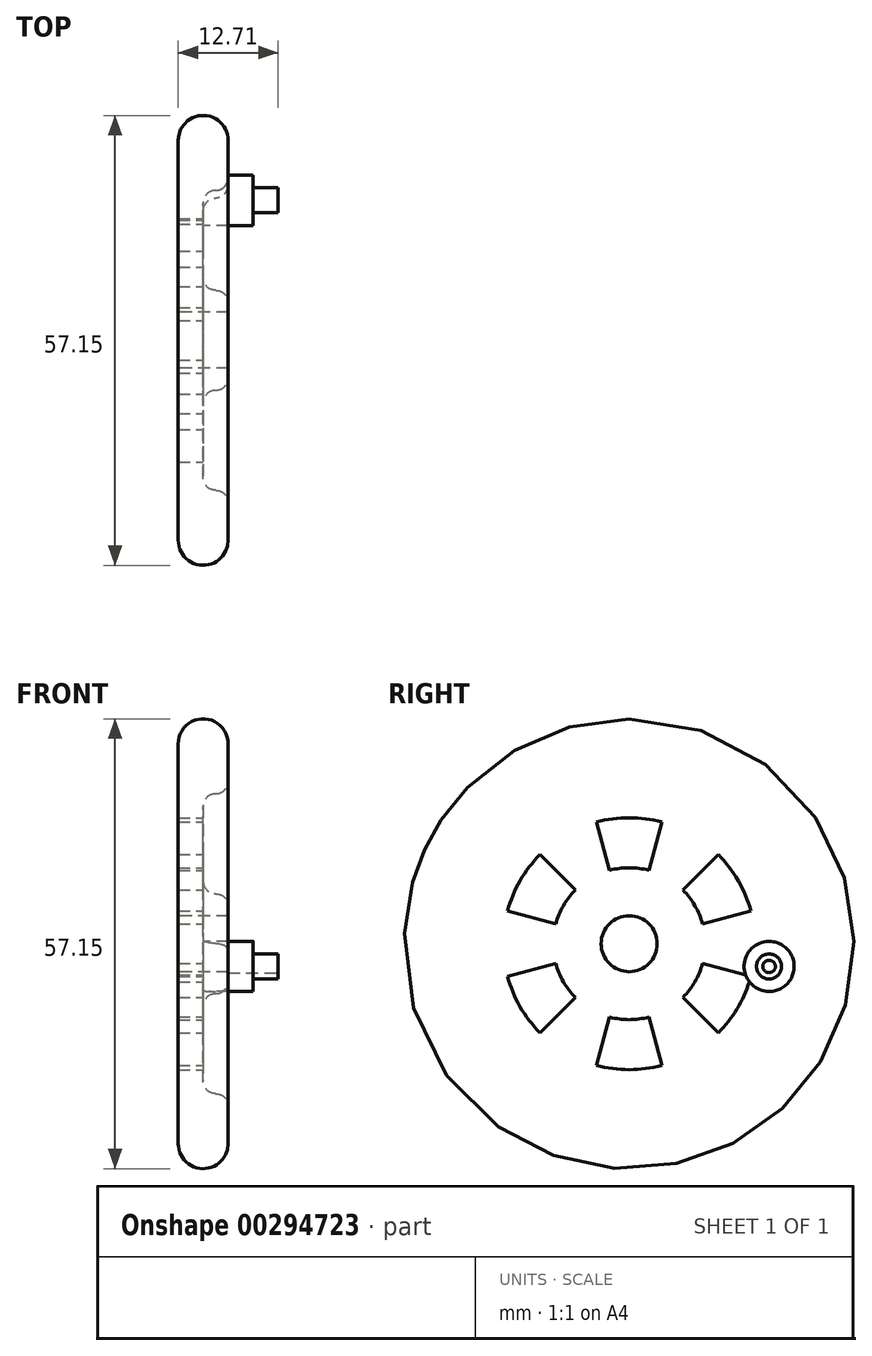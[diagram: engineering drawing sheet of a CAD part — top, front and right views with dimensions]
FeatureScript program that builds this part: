
annotation { "Feature Type Name" : "Feature", "Feature Type Description" : "" }
export const myFeature = defineFeature(function(context is Context, id is Id, definition is map)
    precondition{}
    {
        {
            var Q0;
            Q0=qCreatedBy(makeId("Top.planeOp"),FACE);
            var sketch = newSketch(context, id + "F0", { "sketchPlane" : qUnion([Q0])});
            skArc(sketch, "E0", {"start": v(-3.18, -11.95) * mm, "mid": v(0, -15.13) * mm, "end": v(3.18, -11.95) * mm});
            skLineSegment(sketch, "E1", {"start": v(0, 5.5) * mm, "end": v(0, -4) * mm});
            skLineSegment(sketch, "E2", {"start": v(1.6, -5.6) * mm, "end": v(3.18, -5.6) * mm});
            skLineSegment(sketch, "E3", {"start": v(3.18, -5.6) * mm, "end": v(3.18, -11.95) * mm});
            skLineSegment(sketch, "E4", {"start": v(-3.18, 9.9) * mm, "end": v(-3.18, 11.85) * mm, "construction": true});
            skLineSegment(sketch, "E5", {"start": v(-1.57, 13.45) * mm, "end": v(3.18, 13.45) * mm, "construction": true});
            skLineSegment(sketch, "E6", {"start": v(3.17, 13.45) * mm, "end": v(3.17, 9.9) * mm, "construction": true});
            skPoint(sketch, "E7.visualSharp", {"position": v(-3.18, 9.9) * mm});
            skPoint(sketch, "E8.visualSharp", {"position": v(0, -5.6) * mm});
            skArc(sketch, "E8.filletArc", {"start": v(0, -4) * mm, "mid": v(0.47, -5.13) * mm, "end": v(1.6, -5.6) * mm});
            skPoint(sketch, "E9.visualSharp", {"position": v(3.17, 7.1) * mm});
            skPoint(sketch, "E10.visualSharp", {"position": v(-3.18, 13.45) * mm});
            skLineSegment(sketch, "E11", {"start": v(-1.57, 13.45) * mm, "end": v(-3.18, 13.45) * mm, "construction": true});
            skLineSegment(sketch, "E12", {"start": v(-3.18, 11.85) * mm, "end": v(-3.18, 13.45) * mm, "construction": true});
            skLineSegment(sketch, "E13", {"start": v(3.18, 9.9) * mm, "end": v(3.17, 7.1) * mm});
            skLineSegment(sketch, "E14", {"start": v(1.6, 7.1) * mm, "end": v(3.17, 7.1) * mm});
            skPoint(sketch, "E15.visualSharp", {"position": v(0, 7.1) * mm});
            skArc(sketch, "E15.filletArc", {"start": v(1.6, 7.1) * mm, "mid": v(0.47, 6.63) * mm, "end": v(0, 5.5) * mm});
            skLineSegment(sketch, "E16", {"start": v(-3.18, 9.9) * mm, "end": v(3.17, 9.9) * mm});
            skLineSegment(sketch, "E17", {"start": v(-3.18, 9.9) * mm, "end": v(-3.17, -11.95) * mm});
            skSolve(sketch);
        }
        {
            var Q0;
            Q0=makeQuery(id+"F0.imprint","IMPRINT",FACE,{"disambiguationData":[TD([[makeQuery(id+"F0.imprint","IMPRINT",EDGE,{"derivedFrom":sQuery(id+"F0.wireOp",EDGE,"E0")}),1.0]])]});
            var Q1;
            Q1=sQuery(id+"F0.wireOp",EDGE,"E5");
            revolve(context, id + "F1", {"entities" : qUnion([Q0]), "axis" : qUnion([Q1]), "revolveType" : RevolveType.FULL});
        }
        {
            var Q0;
            Q0=makeQuery(id+"F1.opRevolve","SWEPT_FACE",FACE,{"disambiguationData":[OSD([sQuery(id+"F0.wireOp",EDGE,"E3")])]});
            var Q1;
            Q1=makeQuery(id+"F1.opRevolve","SWEPT_EDGE",EDGE,{"disambiguationData":[OSD([sQuery(id+"F0.wireOp",EDGE,"E13"),sQuery(id+"F0.wireOp",EDGE,"E14")])]});
            fillet(context, id + "F2", {"entities" : qUnion([Q0, Q1]), "radius" : 1.6 * mm, "tangentPropagation" : true, "allowEdgeOverflow" : false});
        }
        {
            var Q0;
            Q0=makeQuery(id+"F1.opRevolve","SWEPT_FACE",FACE,{"disambiguationData":[OSD([sQuery(id+"F0.wireOp",EDGE,"E1")])]});
            var sketch = newSketch(context, id + "F3", { "sketchPlane" : qUnion([Q0])});
            skPoint(sketch, "E18", {"position": v(13.45, 0) * mm});
            skPoint(sketch, "E19.center.orphan", {"position": v(31.23, -2.9) * mm});
            skCircle(sketch, "E20", {"center": v(31.23, -2.9) * mm, "radius": 3.18 * mm});
            skSolve(sketch);
        }
        {
            var Q0;
            {var subQ0=sQuery(id+"F3.wireOp",EDGE,"E20");var subQ1=makeQuery(id+"F1.opRevolve","SWEPT_EDGE",EDGE,{"disambiguationData":[OSD([sQuery(id+"F0.wireOp",EDGE,"E1"),sQuery(id+"F0.wireOp",EDGE,"E8.filletArc")])]});var subQ2=makeQuery(id+"F3.imprint","INTERSECT",VERTEX,{"disambiguationData":[OD(0.0)],"derivedFrom":[subQ1,subQ0]});Q0=makeQuery(id+"F3.imprint","IMPRINT",FACE,{"disambiguationData":[TD([[makeQuery(id+"F3.imprint","IMPRINT",EDGE,{"disambiguationData":[TD([[subQ2,-1.0]])],"derivedFrom":subQ0}),1.0]])]});}
            var Q1;
            {var subQ0=sQuery(id+"F3.wireOp",EDGE,"E20");var subQ1=makeQuery(id+"F1.opRevolve","SWEPT_EDGE",EDGE,{"disambiguationData":[OSD([sQuery(id+"F0.wireOp",EDGE,"E1"),sQuery(id+"F0.wireOp",EDGE,"E8.filletArc")])]});var subQ2=makeQuery(id+"F3.imprint","INTERSECT",VERTEX,{"disambiguationData":[OD(0.0)],"derivedFrom":[subQ1,subQ0]});Q1=makeQuery(id+"F3.imprint","IMPRINT",FACE,{"disambiguationData":[TD([[makeQuery(id+"F3.imprint","IMPRINT",EDGE,{"disambiguationData":[TD([[subQ2,1.0]])],"derivedFrom":subQ0}),1.0]])]});}
            extrude(context, id + "F4", {"entities" : qUnion([Q0, Q1]), "operationType" : NewBodyOperationType.ADD, "depth" : 6.35 * mm});
        }
        {
            var Q0;
            Q0=makeQuery(id+"F4.opExtrude","CAP_FACE",FACE,{"disambiguationData":[OSD([sQuery(id+"F3.wireOp",EDGE,"E20")])],"isStart":false});
            var sketch = newSketch(context, id + "F5", { "sketchPlane" : qUnion([Q0])});
            skCircle(sketch, "E21", {"center": v(31.23, -2.9) * mm, "radius": 1.59 * mm});
            skSolve(sketch);
        }
        {
            var Q0;
            Q0=makeQuery(id+"F5.imprint","IMPRINT",FACE,{"disambiguationData":[TD([[makeQuery(id+"F5.imprint","IMPRINT",EDGE,{"derivedFrom":sQuery(id+"F5.wireOp",EDGE,"E21")}),1.0]])]});
            extrude(context, id + "F6", {"entities" : qUnion([Q0]), "operationType" : NewBodyOperationType.ADD, "depth" : 3.17 * mm});
        }
        {
            var Q0;
            Q0=makeQuery(id+"F6.opExtrude","CAP_FACE",FACE,{"disambiguationData":[OSD([sQuery(id+"F5.wireOp",EDGE,"E21")])],"isStart":false});
            var sketch = newSketch(context, id + "F7", { "sketchPlane" : qUnion([Q0])});
            skCircle(sketch, "E22", {"center": v(31.23, -2.9) * mm, "radius": 0.8 * mm});
            skSolve(sketch);
        }
        {
            var Q0;
            Q0=makeQuery(id+"F7.imprint","IMPRINT",FACE,{"disambiguationData":[TD([[makeQuery(id+"F7.imprint","IMPRINT",EDGE,{"derivedFrom":sQuery(id+"F7.wireOp",EDGE,"E22")}),1.0]])]});
            extrude(context, id + "F8", {"entities" : qUnion([Q0]), "operationType" : NewBodyOperationType.REMOVE, "oppositeDirection" : true, "depth" : 6.35 * mm});
        }
        {
            var Q0;
            Q0=makeQuery(id+"F1.opRevolve","SWEPT_FACE",FACE,{"disambiguationData":[OSD([sQuery(id+"F0.wireOp",EDGE,"E1")])]});
            var sketch = newSketch(context, id + "F9", { "sketchPlane" : qUnion([Q0])});
            skArc(sketch, "E23", {"start": v(15.95, 9.32) * mm, "mid": v(13.45, 9.65) * mm, "end": v(10.95, 9.32) * mm});
            skArc(sketch, "E24", {"start": v(17.6, 15.46) * mm, "mid": v(13.45, 16) * mm, "end": v(9.3, 15.46) * mm});
            skLineSegment(sketch, "E25", {"start": v(15.95, 9.32) * mm, "end": v(17.6, 15.46) * mm});
            skLineSegment(sketch, "E26", {"start": v(17.6, 15.46) * mm, "end": v(15.95, 9.32) * mm});
            skLineSegment(sketch, "E27", {"start": v(10.95, 9.32) * mm, "end": v(9.3, 15.46) * mm});
            skArc(sketch, "E28.1.0", {"start": v(2.13, 11.32) * mm, "mid": v(-0.4, 8) * mm, "end": v(-2, 4.14) * mm});
            skLineSegment(sketch, "E28.1.1", {"start": v(4.13, 2.5) * mm, "end": v(-2, 4.14) * mm});
            skArc(sketch, "E28.1.2", {"start": v(6.62, 6.82) * mm, "mid": v(5.09, 4.83) * mm, "end": v(4.13, 2.5) * mm});
            skLineSegment(sketch, "E28.1.3", {"start": v(6.62, 6.82) * mm, "end": v(2.13, 11.32) * mm});
            skArc(sketch, "E28.2.0", {"start": v(-2, -4.14) * mm, "mid": v(-0.4, -8) * mm, "end": v(2.13, -11.32) * mm});
            skLineSegment(sketch, "E28.2.1", {"start": v(6.62, -6.82) * mm, "end": v(2.13, -11.32) * mm});
            skArc(sketch, "E28.2.2", {"start": v(4.13, -2.5) * mm, "mid": v(5.09, -4.83) * mm, "end": v(6.62, -6.82) * mm});
            skLineSegment(sketch, "E28.2.3", {"start": v(4.13, -2.5) * mm, "end": v(-2, -4.14) * mm});
            skArc(sketch, "E29.1.3.0", {"start": v(9.3, -15.46) * mm, "mid": v(13.45, -16) * mm, "end": v(17.6, -15.46) * mm});
            skLineSegment(sketch, "E29.4.3.0", {"start": v(15.95, -9.32) * mm, "end": v(17.6, -15.46) * mm});
            skArc(sketch, "E29.7.3.0", {"start": v(10.95, -9.32) * mm, "mid": v(13.45, -9.65) * mm, "end": v(15.95, -9.32) * mm});
            skLineSegment(sketch, "E29.11.3.0", {"start": v(10.95, -9.32) * mm, "end": v(9.3, -15.46) * mm});
            skArc(sketch, "E29.1.4.0", {"start": v(24.76, -11.32) * mm, "mid": v(27.3, -8) * mm, "end": v(28.9, -4.14) * mm});
            skLineSegment(sketch, "E29.4.4.0", {"start": v(22.77, -2.5) * mm, "end": v(28.9, -4.14) * mm});
            skArc(sketch, "E29.7.4.0", {"start": v(20.27, -6.82) * mm, "mid": v(21.8, -4.83) * mm, "end": v(22.77, -2.5) * mm});
            skLineSegment(sketch, "E29.11.4.0", {"start": v(20.27, -6.82) * mm, "end": v(24.76, -11.32) * mm});
            skArc(sketch, "E29.1.5.0", {"start": v(28.9, 4.14) * mm, "mid": v(27.3, 8) * mm, "end": v(24.76, 11.32) * mm});
            skLineSegment(sketch, "E29.4.5.0", {"start": v(20.27, 6.82) * mm, "end": v(24.76, 11.32) * mm});
            skArc(sketch, "E29.7.5.0", {"start": v(22.77, 2.5) * mm, "mid": v(21.8, 4.83) * mm, "end": v(20.27, 6.82) * mm});
            skLineSegment(sketch, "E29.11.5.0", {"start": v(22.77, 2.5) * mm, "end": v(28.9, 4.14) * mm});
            skSolve(sketch);
        }
        {
            var Q0;
            Q0=makeQuery(id+"F9.imprint","IMPRINT",FACE,{"disambiguationData":[TD([[makeQuery(id+"F9.imprint","IMPRINT",EDGE,{"derivedFrom":sQuery(id+"F9.wireOp",EDGE,"E23")}),-1.0]])]});
            var Q1;
            Q1=makeQuery(id+"F9.imprint","IMPRINT",FACE,{"disambiguationData":[TD([[makeQuery(id+"F9.imprint","IMPRINT",EDGE,{"derivedFrom":sQuery(id+"F9.wireOp",EDGE,"E28.1.0")}),1.0]])]});
            var Q2;
            Q2=makeQuery(id+"F9.imprint","IMPRINT",FACE,{"disambiguationData":[TD([[makeQuery(id+"F9.imprint","IMPRINT",EDGE,{"derivedFrom":sQuery(id+"F9.wireOp",EDGE,"E28.2.0")}),1.0]])]});
            var Q3;
            Q3=makeQuery(id+"F9.imprint","IMPRINT",FACE,{"disambiguationData":[TD([[makeQuery(id+"F9.imprint","IMPRINT",EDGE,{"derivedFrom":sQuery(id+"F9.wireOp",EDGE,"E29.1.3.0")}),1.0]])]});
            var Q4;
            {var subQ0=sQuery(id+"F9.wireOp",EDGE,"E29.7.4.0");Q4=makeQuery(id+"F9.imprint","IMPRINT",FACE,{"disambiguationData":[TD([[makeQuery(id+"F9.imprint","IMPRINT",EDGE,{"derivedFrom":subQ0}),-1.0]])]});}
            var Q5;
            Q5=makeQuery(id+"F9.imprint","IMPRINT",FACE,{"disambiguationData":[TD([[makeQuery(id+"F9.imprint","IMPRINT",EDGE,{"derivedFrom":sQuery(id+"F9.wireOp",EDGE,"E29.1.5.0")}),1.0]])]});
            extrude(context, id + "F10", {"entities" : qUnion([Q0, Q1, Q2, Q3, Q4, Q5]), "operationType" : NewBodyOperationType.REMOVE, "oppositeDirection" : true, "depth" : 25.4 * mm});
        }
    });
